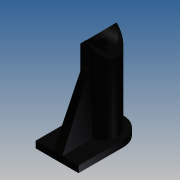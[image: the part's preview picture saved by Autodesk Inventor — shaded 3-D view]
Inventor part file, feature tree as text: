
AUTODESK INVENTOR PART (.ipt)
format: ipt  version: 2013 (Build 170138000, 138)  size: 114,688 bytes
history: native  units: in
note: dims shown in document units (in); Inventor stores cm internally (conversion verified against a paired STEP export)
features: mirror x1, other x1, imported_body x1
ambient origin geometry x8: Origin, YZ Plane, XZ Plane, XY Plane, X Axis, Y Axis, Z Axis, Center Point
feature tree (3):
  mirror  "Mirror3"
  other  "175_filament_feed1"
  imported_body  "Base1"
